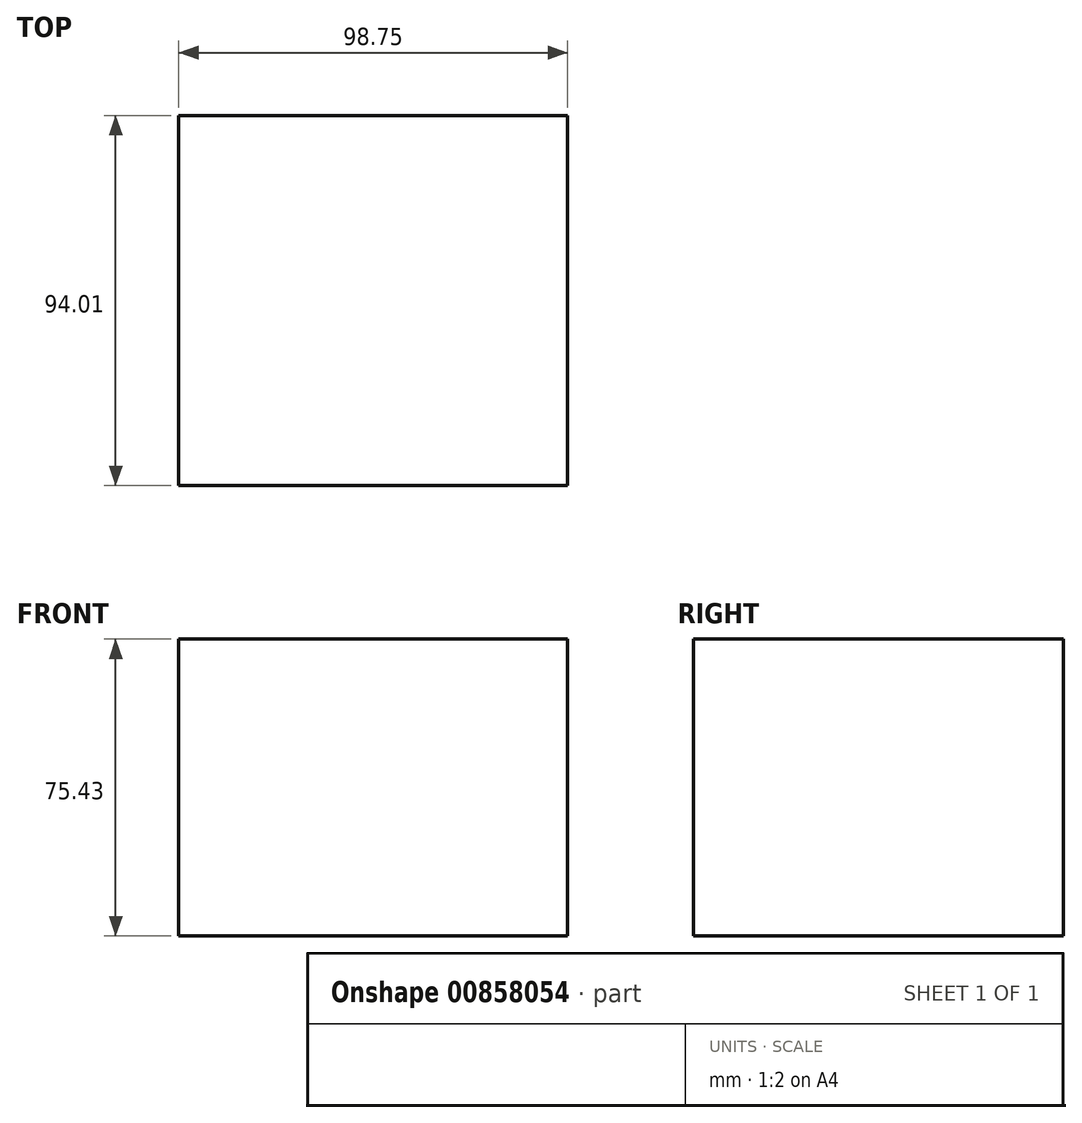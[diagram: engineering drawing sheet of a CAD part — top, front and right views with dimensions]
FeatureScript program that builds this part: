
annotation { "Feature Type Name" : "Feature", "Feature Type Description" : "" }
export const myFeature = defineFeature(function(context is Context, id is Id, definition is map)
    precondition{}
    {
        {
            var Q0;
            Q0=qCreatedBy(makeId("Top.planeOp"),FACE);
            var sketch = newSketch(context, id + "F0", { "sketchPlane" : qUnion([Q0])});
            skLineSegment(sketch, "E0.bottom", {"start": v(48.44, -55.22) * mm, "end": v(-50.3, -55.22) * mm});
            skLineSegment(sketch, "E0.top", {"start": v(48.44, 38.79) * mm, "end": v(-50.3, 38.79) * mm});
            skLineSegment(sketch, "E0.left", {"start": v(48.44, -55.22) * mm, "end": v(48.44, 38.79) * mm});
            skLineSegment(sketch, "E0.right", {"start": v(-50.3, -55.22) * mm, "end": v(-50.3, 38.79) * mm});
            skSolve(sketch);
        }
        {
            var Q0;
            Q0 = qSketchRegion(id + "F0", true);
            extrude(context, id + "F1", {"entities" : qUnion([Q0]), "depth" : 75.43 * mm, "offsetDistance" : 25.4 * mm});
        }
    });
